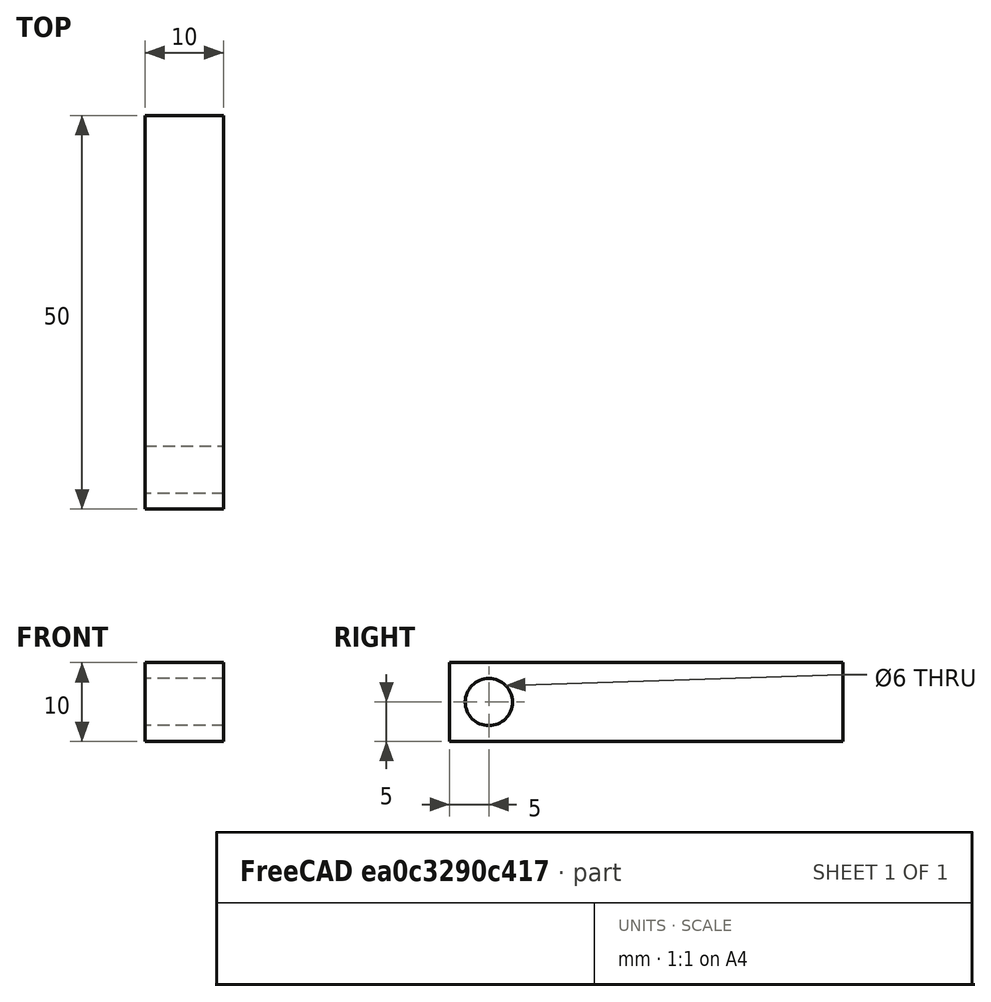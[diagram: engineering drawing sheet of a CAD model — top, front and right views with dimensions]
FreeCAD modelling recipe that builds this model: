
FCSTD DOCUMENT  (FreeCAD 0.21R33668 +26 (Git))
Label: Piece001
License: All rights reserved
LicenseURL: http://en.wikipedia.org/wiki/All_rights_reserved
objects: Sketcher::SketchObject×1, PartDesign::Pad×1, PartDesign::Body×1
note: 4 computed .brp shape members not serialized (recipe doc carries the construction recipe); baked Part::Feature solids carry a one-line shape summary decoded from their .brp

FEATURE [Sketcher::SketchObject] Sketch
  FullyConstrained = true
  MapMode = 5
  Placement = pos=(0,0,0) rot=(0.57735,0.57735,0.57735;2.0944rad)
  Support = -> [YZ_Plane]
  sketch-geometry (5):
    g0: LineSegment StartX=-5 StartY=-5 StartZ=0 EndX=45 EndY=-5 EndZ=0
    g1: LineSegment StartX=45 StartY=-5 StartZ=0 EndX=45 EndY=5 EndZ=0
    g2: LineSegment StartX=45 StartY=5 StartZ=0 EndX=-5 EndY=5 EndZ=0
    g3: LineSegment StartX=-5 StartY=5 StartZ=0 EndX=-5 EndY=-5 EndZ=0
    g4: Circle CenterX=0 CenterY=0 CenterZ=0 NormalX=0 NormalY=0 NormalZ=1 AngleXU=0 Radius=3
  constraints (14):
    c: Coincident(g0,g1)
    c: Coincident(g1,g2)
    c: Coincident(g2,g3)
    c: Coincident(g3,g0)
    c: Coincident(g4,g-1)
    c: Radius(g4) = 3
    c: Parallel(g2,g0)
    c: Parallel(g3,g1)
    c: Perpendicular(g1,g2)
    c: Distance(g4,g2) = 5
    c: Distance(g2,g1) = 50
    c: Distance(g1,g0) = 10
    c: Distance(g4,g3) = 5
    c: Angle(g-1,g2) = 0
FEATURE [PartDesign::Pad] Pad
  Direction = (1,-2e-16,3e-16)
  Length = 10
  Length2 = 10
  Placement = pos=(0,0,0) rot=(1,1,1;2.0944rad)
  Profile = -> Sketch
  ReferenceAxis = -> Sketch [N_Axis]
  Type = 0
FEATURE [PartDesign::Body] Body  label="Corps"
  Group = -> [Sketch,Pad]
  Origin = -> Origin
  Tip = -> Pad
